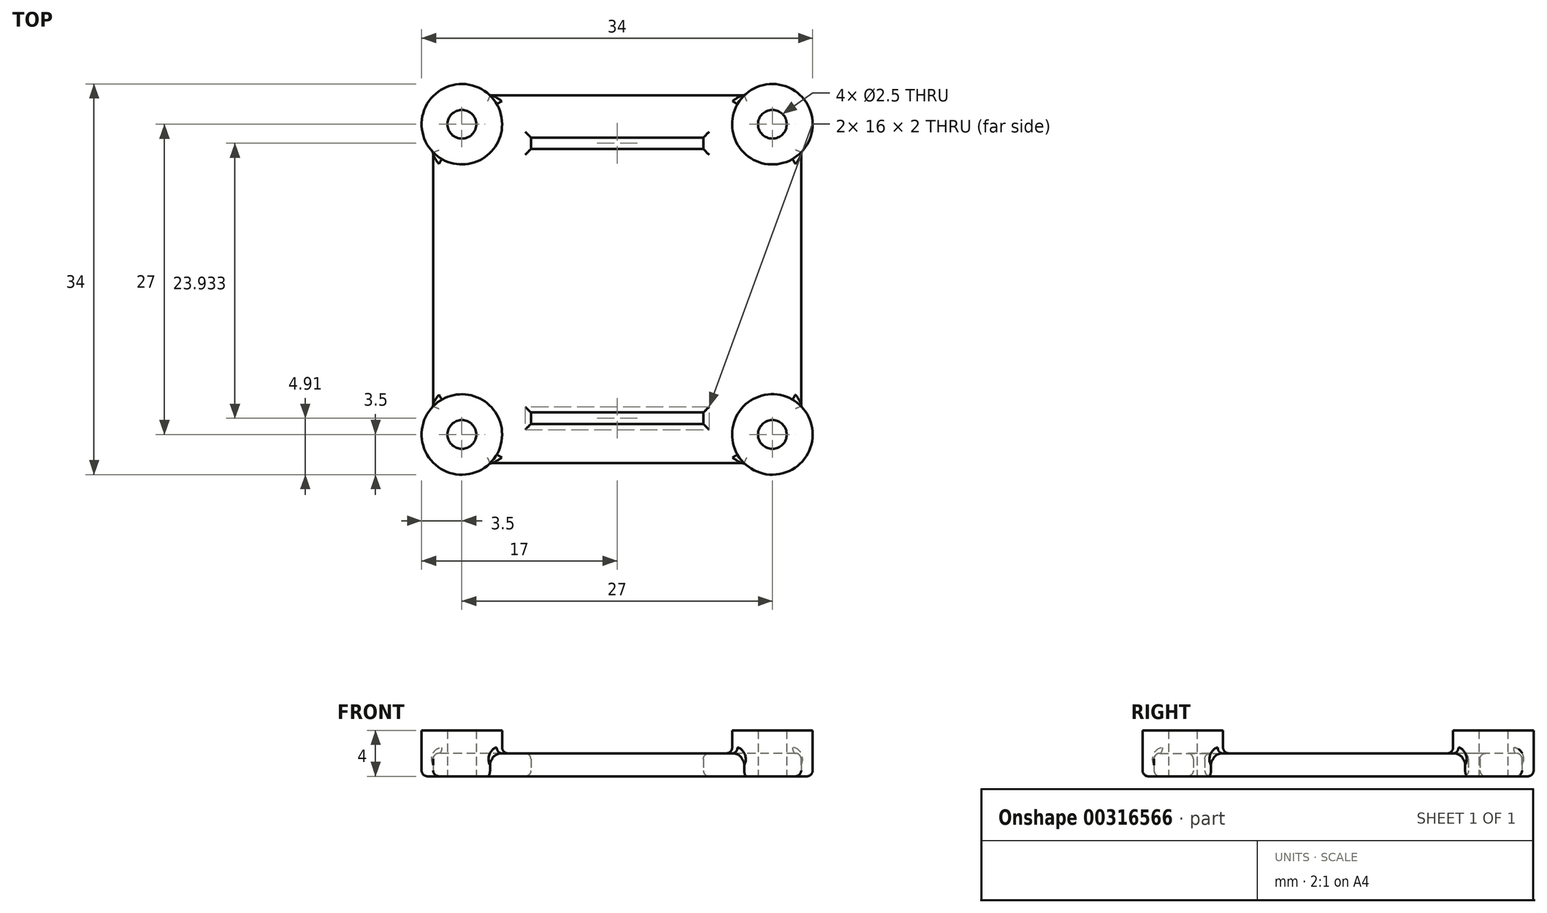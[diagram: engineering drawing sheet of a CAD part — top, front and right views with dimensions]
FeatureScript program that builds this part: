
annotation { "Feature Type Name" : "Feature", "Feature Type Description" : "" }
export const myFeature = defineFeature(function(context is Context, id is Id, definition is map)
    precondition{}
    {
        {
            var Q0;
            Q0=qCreatedBy(makeId("Top.planeOp"),FACE);
            var sketch = newSketch(context, id + "F0", { "sketchPlane" : qUnion([Q0])});
            skLineSegment(sketch, "E0.bottom", {"start": v(13.5, -13.5) * mm, "end": v(-13.5, -13.5) * mm, "construction": true});
            skLineSegment(sketch, "E0.top", {"start": v(13.5, 13.5) * mm, "end": v(-13.5, 13.5) * mm, "construction": true});
            skLineSegment(sketch, "E0.left", {"start": v(13.5, -13.5) * mm, "end": v(13.5, 13.5) * mm, "construction": true});
            skLineSegment(sketch, "E0.right", {"start": v(-13.5, -13.5) * mm, "end": v(-13.5, 13.5) * mm, "construction": true});
            skPoint(sketch, "E0.middle", {"position": v(0, 0) * mm});
            skCircle(sketch, "E1", {"center": v(-13.5, 13.5) * mm, "radius": 1.25 * mm});
            skCircle(sketch, "E2", {"center": v(13.5, 13.5) * mm, "radius": 1.25 * mm});
            skCircle(sketch, "E3", {"center": v(13.5, -13.5) * mm, "radius": 1.25 * mm});
            skCircle(sketch, "E4", {"center": v(-13.5, -13.5) * mm, "radius": 1.25 * mm});
            skCircle(sketch, "E5", {"center": v(-13.5, 13.5) * mm, "radius": 3.5 * mm});
            skCircle(sketch, "E6", {"center": v(13.5, 13.5) * mm, "radius": 3.5 * mm});
            skLineSegment(sketch, "E7", {"start": v(11.05, 16) * mm, "end": v(-11.05, 16) * mm});
            skCircle(sketch, "E8", {"center": v(-13.5, -13.5) * mm, "radius": 3.5 * mm});
            skCircle(sketch, "E9", {"center": v(13.5, -13.5) * mm, "radius": 3.5 * mm});
            skLineSegment(sketch, "E10", {"start": v(16, -11.05) * mm, "end": v(16, 11.05) * mm});
            skLineSegment(sketch, "E11", {"start": v(11.05, -16) * mm, "end": v(-11.05, -16) * mm});
            skLineSegment(sketch, "E12", {"start": v(-16, -11.05) * mm, "end": v(-16, 11.05) * mm});
            skLineSegment(sketch, "E13", {"start": v(-7.5, 12.34) * mm, "end": v(7.5, 12.34) * mm});
            skLineSegment(sketch, "E14", {"start": v(7.5, 12.34) * mm, "end": v(7.5, 11.34) * mm});
            skLineSegment(sketch, "E15", {"start": v(-7.5, 12.34) * mm, "end": v(-7.5, 11.34) * mm});
            skLineSegment(sketch, "E16", {"start": v(-7.5, 11.34) * mm, "end": v(7.5, 11.34) * mm});
            skLineSegment(sketch, "E17", {"start": v(-7.5, -12.6) * mm, "end": v(7.5, -12.6) * mm});
            skLineSegment(sketch, "E18", {"start": v(-7.5, -12.6) * mm, "end": v(-7.5, -11.6) * mm});
            skLineSegment(sketch, "E19", {"start": v(-7.5, -11.6) * mm, "end": v(7.5, -11.6) * mm});
            skLineSegment(sketch, "E20", {"start": v(7.5, -11.6) * mm, "end": v(7.5, -12.6) * mm});
            skSolve(sketch);
        }
        {
            var Q0;
            Q0 = qSketchRegion(id + "F0", true);
            extrude(context, id + "F1", {"entities" : qUnion([Q0]), "depth" : 2 * mm});
        }
        {
            var Q0;
            Q0=makeQuery(id+"F1.opExtrude","CAP_FACE",FACE,{"disambiguationData":[OSD([sQuery(id+"F0.wireOp",EDGE,"XYMYm1aW-laoe-EzPC-uc5R-h6hxVWD1be2q.bottom"),sQuery(id+"F0.wireOp",EDGE,"XYMYm1aW-laoe-EzPC-uc5R-h6hxVWD1be2q.top"),sQuery(id+"F0.wireOp",EDGE,"XYMYm1aW-laoe-EzPC-uc5R-h6hxVWD1be2q.left"),sQuery(id+"F0.wireOp",EDGE,"XYMYm1aW-laoe-EzPC-uc5R-h6hxVWD1be2q.right"),sQuery(id+"F0.wireOp",EDGE,"4e9d475b-7e58-459e-b837-5ff324b879ee.filletArc"),sQuery(id+"F0.wireOp",EDGE,"1084adef-c6ab-4bce-84d3-c1634e60802e.filletArc"),sQuery(id+"F0.wireOp",EDGE,"ce6bfa69-b2e9-4cad-8ce9-c769d40bcedd.filletArc"),sQuery(id+"F0.wireOp",EDGE,"81c454f9-fd5b-4531-b486-0c800fde98c0.filletArc"),sQuery(id+"F0.wireOp",EDGE,"E1"),sQuery(id+"F0.wireOp",EDGE,"E2"),sQuery(id+"F0.wireOp",EDGE,"E3"),sQuery(id+"F0.wireOp",EDGE,"E4")])],"isStart":false});
            var sketch = newSketch(context, id + "F2", { "sketchPlane" : qUnion([Q0])});
            skCircle(sketch, "E21", {"center": v(-13.5, 13.5) * mm, "radius": 3.5 * mm});
            skCircle(sketch, "E22", {"center": v(13.5, 13.5) * mm, "radius": 3.5 * mm});
            skCircle(sketch, "E23", {"center": v(13.5, -13.5) * mm, "radius": 3.5 * mm});
            skCircle(sketch, "E24", {"center": v(-13.5, -13.5) * mm, "radius": 3.5 * mm});
            skCircle(sketch, "E25.0", {"center": v(-13.5, 13.5) * mm, "radius": 1.25 * mm});
            skCircle(sketch, "E26.0", {"center": v(13.5, 13.5) * mm, "radius": 1.25 * mm});
            skCircle(sketch, "E27.0", {"center": v(13.5, -13.5) * mm, "radius": 1.25 * mm});
            skCircle(sketch, "E28.0", {"center": v(-13.5, -13.5) * mm, "radius": 1.25 * mm});
            skSolve(sketch);
        }
        {
            var Q0;
            Q0 = qSketchRegion(id + "F2", true);
            extrude(context, id + "F3", {"entities" : qUnion([Q0]), "operationType" : NewBodyOperationType.ADD, "depth" : 2 * mm});
        }
        {
            var Q0;
            Q0=makeQuery(id+"F1.opExtrude","CAP_EDGE",EDGE,{"disambiguationData":[OSD([sQuery(id+"F0.wireOp",EDGE,"E6")])],"isStart":true});
            var Q1;
            Q1=makeQuery(id+"F1.opExtrude","CAP_EDGE",EDGE,{"disambiguationData":[OSD([sQuery(id+"F0.wireOp",EDGE,"E10")])],"isStart":true});
            var Q2;
            Q2=makeQuery(id+"F1.opExtrude","CAP_EDGE",EDGE,{"disambiguationData":[OSD([sQuery(id+"F0.wireOp",EDGE,"E9")])],"isStart":true});
            var Q3;
            Q3=makeQuery(id+"F1.opExtrude","CAP_EDGE",EDGE,{"disambiguationData":[OSD([sQuery(id+"F0.wireOp",EDGE,"E11")])],"isStart":true});
            var Q4;
            Q4=makeQuery(id+"F1.opExtrude","CAP_EDGE",EDGE,{"disambiguationData":[OSD([sQuery(id+"F0.wireOp",EDGE,"E8")])],"isStart":true});
            var Q5;
            Q5=makeQuery(id+"F1.opExtrude","CAP_EDGE",EDGE,{"disambiguationData":[OSD([sQuery(id+"F0.wireOp",EDGE,"E12")])],"isStart":true});
            var Q6;
            Q6=makeQuery(id+"F1.opExtrude","CAP_EDGE",EDGE,{"disambiguationData":[OSD([sQuery(id+"F0.wireOp",EDGE,"E5")])],"isStart":true});
            var Q7;
            Q7=makeQuery(id+"F1.opExtrude","CAP_EDGE",EDGE,{"disambiguationData":[OSD([sQuery(id+"F0.wireOp",EDGE,"E7")])],"isStart":true});
            fillet(context, id + "F4", {"entities" : qUnion([Q0, Q1, Q2, Q3, Q4, Q5, Q6, Q7]), "radius" : 0.5 * mm, "tangentPropagation" : true, "allowEdgeOverflow" : false});
        }
        {
            var Q0;
            Q0=makeQuery(id+"F1.opExtrude","CAP_FACE",FACE,{"disambiguationData":[OSD([sQuery(id+"F0.wireOp",EDGE,"XYMYm1aW-laoe-EzPC-uc5R-h6hxVWD1be2q.bottom"),sQuery(id+"F0.wireOp",EDGE,"XYMYm1aW-laoe-EzPC-uc5R-h6hxVWD1be2q.top"),sQuery(id+"F0.wireOp",EDGE,"XYMYm1aW-laoe-EzPC-uc5R-h6hxVWD1be2q.left"),sQuery(id+"F0.wireOp",EDGE,"XYMYm1aW-laoe-EzPC-uc5R-h6hxVWD1be2q.right"),sQuery(id+"F0.wireOp",EDGE,"4e9d475b-7e58-459e-b837-5ff324b879ee.filletArc"),sQuery(id+"F0.wireOp",EDGE,"1084adef-c6ab-4bce-84d3-c1634e60802e.filletArc"),sQuery(id+"F0.wireOp",EDGE,"ce6bfa69-b2e9-4cad-8ce9-c769d40bcedd.filletArc"),sQuery(id+"F0.wireOp",EDGE,"81c454f9-fd5b-4531-b486-0c800fde98c0.filletArc"),sQuery(id+"F0.wireOp",EDGE,"E1"),sQuery(id+"F0.wireOp",EDGE,"E2"),sQuery(id+"F0.wireOp",EDGE,"E3"),sQuery(id+"F0.wireOp",EDGE,"E4")])],"isStart":false});
            fillet(context, id + "F5", {"entities" : qUnion([Q0]), "radius" : 0.5 * mm, "tangentPropagation" : true, "allowEdgeOverflow" : false});
        }
        {
            var Q0;
            Q0=makeQuery(id+"F1.opExtrude","CAP_EDGE",EDGE,{"disambiguationData":[OSD([sQuery(id+"F0.wireOp",EDGE,"E16")])],"isStart":true});
            var Q1;
            Q1=makeQuery(id+"F1.opExtrude","CAP_EDGE",EDGE,{"disambiguationData":[OSD([sQuery(id+"F0.wireOp",EDGE,"E13")])],"isStart":true});
            var Q2;
            Q2=makeQuery(id+"F1.opExtrude","CAP_EDGE",EDGE,{"disambiguationData":[OSD([sQuery(id+"F0.wireOp",EDGE,"E15")])],"isStart":true});
            var Q3;
            Q3=makeQuery(id+"F1.opExtrude","CAP_EDGE",EDGE,{"disambiguationData":[OSD([sQuery(id+"F0.wireOp",EDGE,"E14")])],"isStart":true});
            var Q4;
            Q4=makeQuery(id+"F1.opExtrude","CAP_EDGE",EDGE,{"disambiguationData":[OSD([sQuery(id+"F0.wireOp",EDGE,"E20")])],"isStart":true});
            var Q5;
            Q5=makeQuery(id+"F1.opExtrude","CAP_EDGE",EDGE,{"disambiguationData":[OSD([sQuery(id+"F0.wireOp",EDGE,"E17")])],"isStart":true});
            var Q6;
            Q6=makeQuery(id+"F1.opExtrude","CAP_EDGE",EDGE,{"disambiguationData":[OSD([sQuery(id+"F0.wireOp",EDGE,"E18")])],"isStart":true});
            var Q7;
            Q7=makeQuery(id+"F1.opExtrude","CAP_EDGE",EDGE,{"disambiguationData":[OSD([sQuery(id+"F0.wireOp",EDGE,"E19")])],"isStart":true});
            fillet(context, id + "F6", {"entities" : qUnion([Q0, Q1, Q2, Q3, Q4, Q5, Q6, Q7]), "radius" : .5 * mm, "tangentPropagation" : true, "allowEdgeOverflow" : false});
        }
    });
